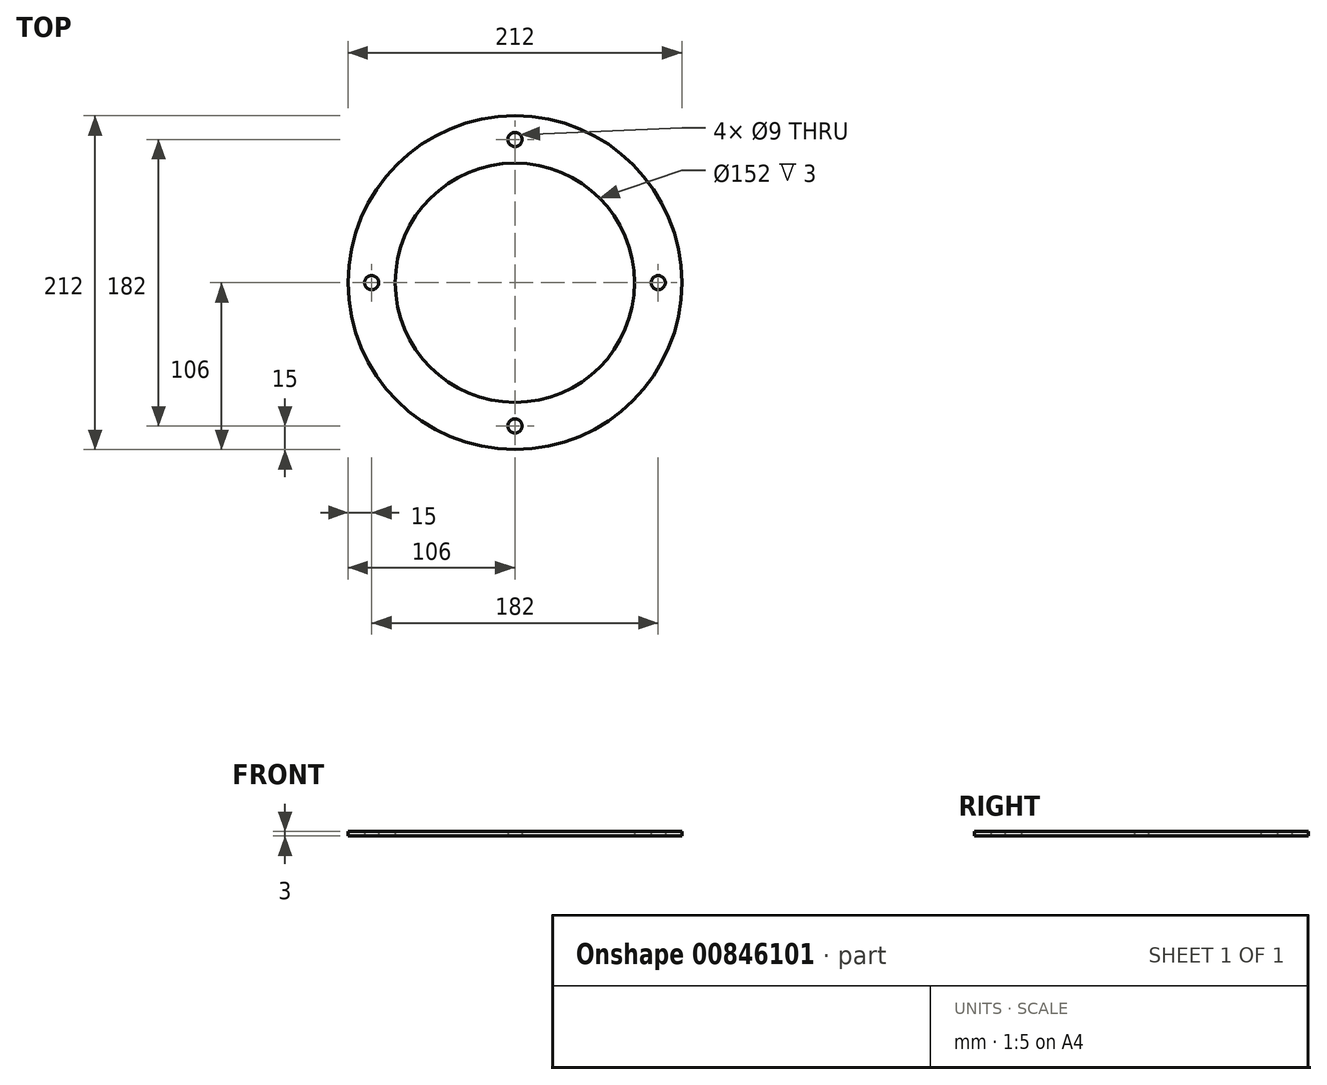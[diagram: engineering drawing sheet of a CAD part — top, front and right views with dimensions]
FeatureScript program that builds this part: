
annotation { "Feature Type Name" : "Feature", "Feature Type Description" : "" }
export const myFeature = defineFeature(function(context is Context, id is Id, definition is map)
    precondition{}
    {
        {
            var Q0;
            Q0=qCreatedBy(makeId("Top.planeOp"),FACE);
            var sketch = newSketch(context, id + "F0", { "sketchPlane" : qUnion([Q0])});
            skCircle(sketch, "E0", {"center": v(0, 0) * mm, "radius": 76 * mm});
            skCircle(sketch, "E1", {"center": v(0, 0) * mm, "radius": 106 * mm});
            skCircle(sketch, "E2", {"center": v(0, 91) * mm, "radius": 4.5 * mm});
            skCircle(sketch, "E3.1.0", {"center": v(-91, 0) * mm, "radius": 4.5 * mm});
            skCircle(sketch, "E3.2.0", {"center": v(0, -91) * mm, "radius": 4.5 * mm});
            skCircle(sketch, "E3.3.0", {"center": v(91, 0) * mm, "radius": 4.5 * mm});
            skSolve(sketch);
        }
        {
            var Q0;
            Q0=makeQuery(id+"F0.imprint","IMPRINT",FACE,{"disambiguationData":[TD([[makeQuery(id+"F0.imprint","IMPRINT",EDGE,{"derivedFrom":sQuery(id+"F0.wireOp",EDGE,"E0")}),-1.0]])]});
            extrude(context, id + "F1", {"entities" : qUnion([Q0]), "depth" : 3 * mm, "offsetDistance" : 25 * mm});
        }
    });
